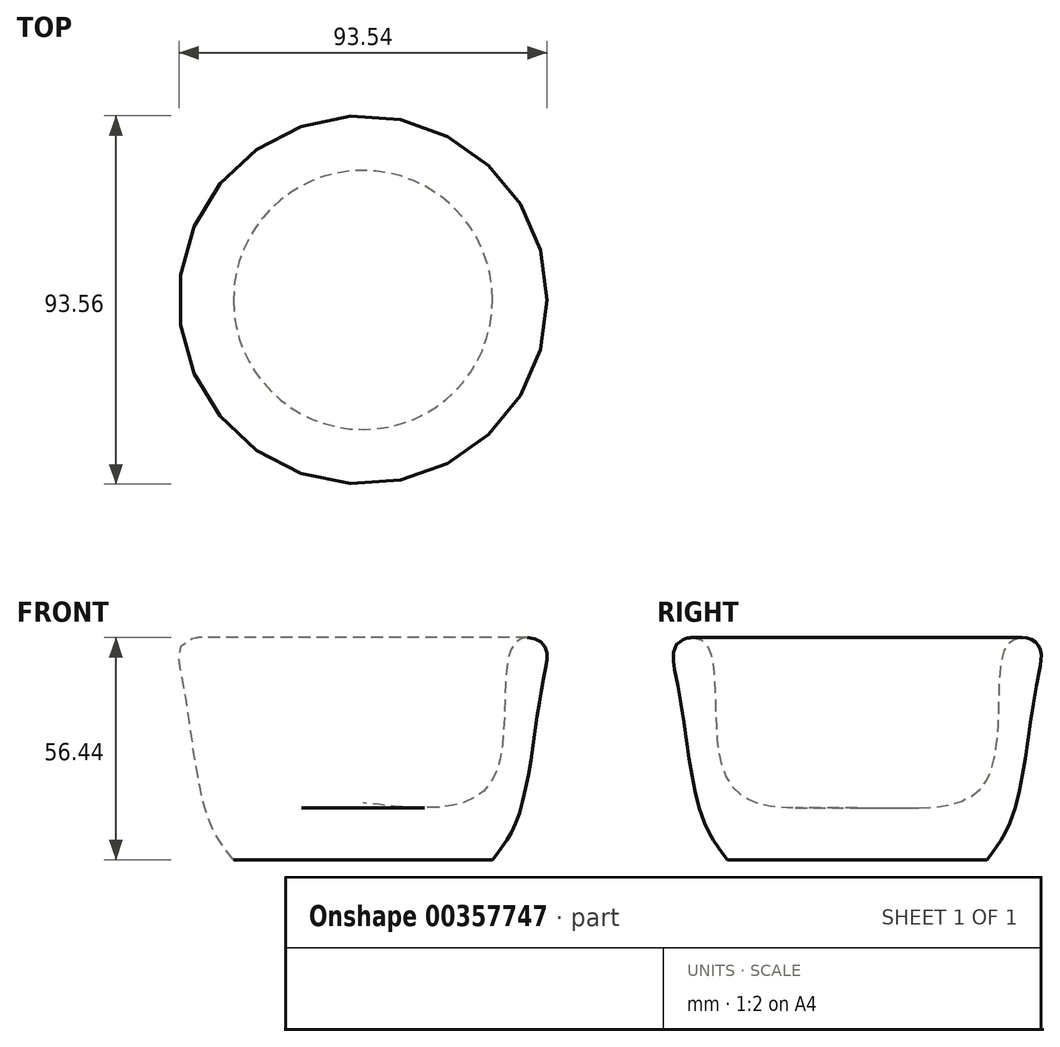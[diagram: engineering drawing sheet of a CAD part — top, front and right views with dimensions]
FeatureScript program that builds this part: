
annotation { "Feature Type Name" : "Feature", "Feature Type Description" : "" }
export const myFeature = defineFeature(function(context is Context, id is Id, definition is map)
    precondition{}
    {
        {
            var Q0;
            Q0=qCreatedBy(makeId("Front.planeOp"),FACE);
            var sketch = newSketch(context, id + "F0", { "sketchPlane" : qUnion([Q0])});
            skLineSegment(sketch, "E0", {"start": v(0, 0) * mm, "end": v(0, 14.44) * mm});
            skLineSegment(sketch, "E1", {"start": v(0, 0) * mm, "end": v(32.9, 0) * mm});
            skFitSpline(sketch, "E2", {"points": [v(32.9, 0) * mm, v(39.7, 11.68) * mm, v(45.47, 43.84) * mm, v(45.72, 54.89) * mm, v(38.43, 54.89) * mm, v(32.9, 20.22) * mm, v(0, 14.44) * mm], "startDerivative": vector(55, 68.4) * mm, "endDerivative": vector(-195.72, 22.28) * mm});
            skSolve(sketch);
        }
        {
            var Q0;
            Q0=makeQuery(id+"F0.imprint","IMPRINT",FACE,{"disambiguationData":[TD([[makeQuery(id+"F0.imprint","IMPRINT",EDGE,{"derivedFrom":sQuery(id+"F0.wireOp",EDGE,"E0")}),-1.0]])]});
            var Q1;
            Q1=sQuery(id+"F0.wireOp",EDGE,"E0");
            revolve(context, id + "F1", {"entities" : qUnion([Q0]), "axis" : qUnion([Q1]), "revolveType" : RevolveType.FULL});
        }
    });
